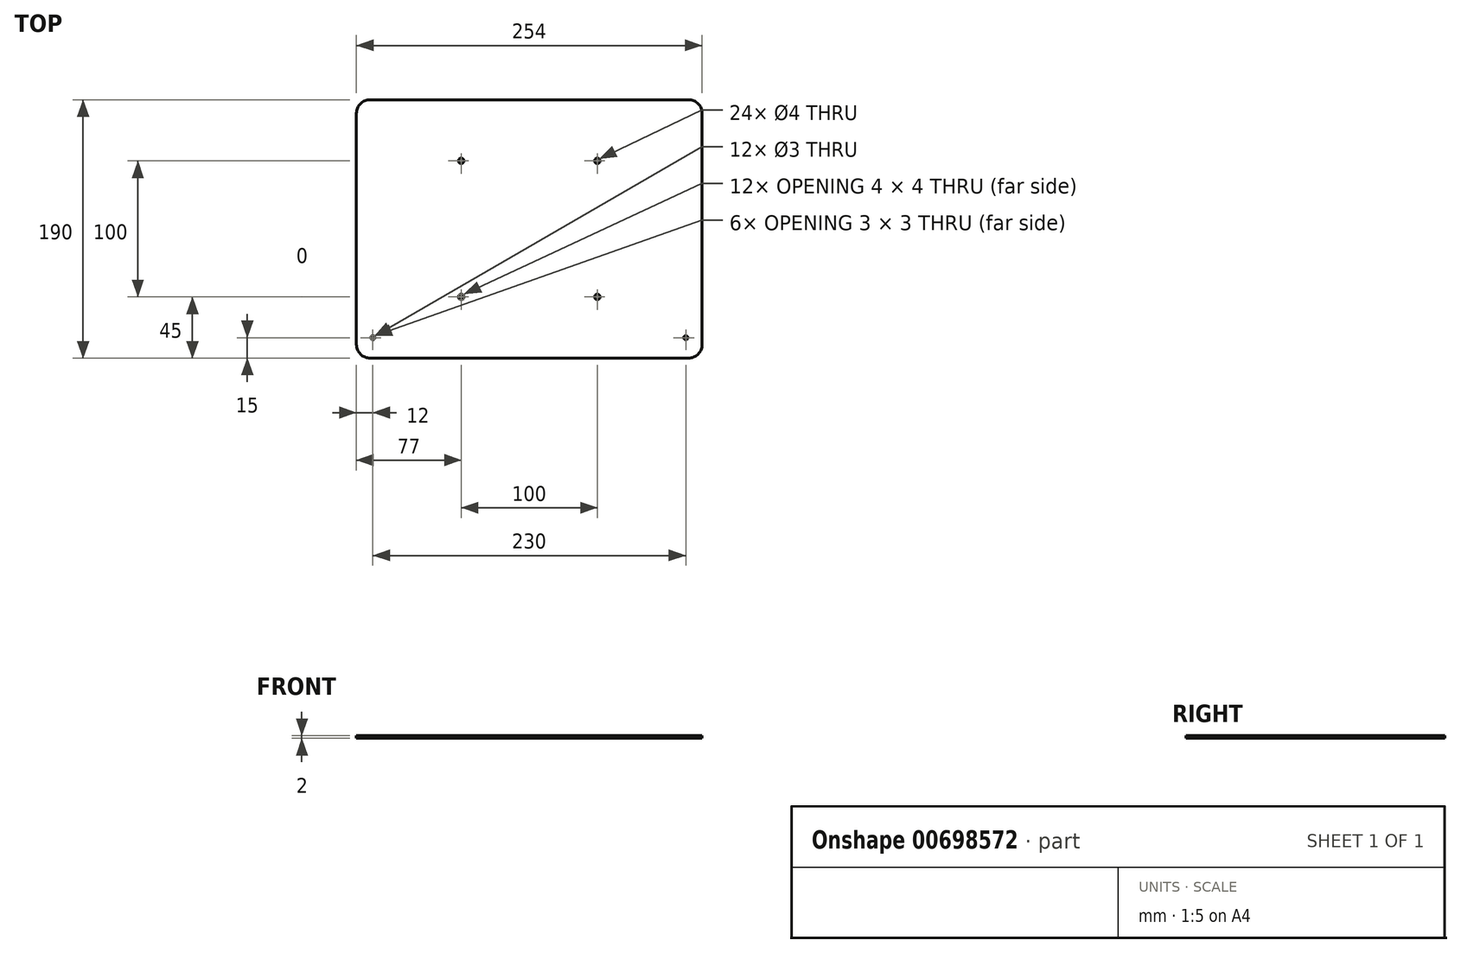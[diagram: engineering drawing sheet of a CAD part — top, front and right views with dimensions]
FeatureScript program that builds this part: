
annotation { "Feature Type Name" : "Feature", "Feature Type Description" : "" }
export const myFeature = defineFeature(function(context is Context, id is Id, definition is map)
    precondition{}
    {
        {
            var Q0;
            Q0=qCreatedBy(makeId("Top.planeOp"),FACE);
            var sketch = newSketch(context, id + "F0", { "sketchPlane" : qUnion([Q0])});
            skLineSegment(sketch, "E0.bottom", {"start": v(-127, 95) * mm, "end": v(127, 95) * mm});
            skLineSegment(sketch, "E0.top", {"start": v(-127, -95) * mm, "end": v(127, -95) * mm});
            skLineSegment(sketch, "E0.left", {"start": v(-127, 95) * mm, "end": v(-127, -95) * mm});
            skLineSegment(sketch, "E0.right", {"start": v(127, 95) * mm, "end": v(127, -95) * mm});
            skPoint(sketch, "E0.middle", {"position": v(0, 0) * mm});
            skSolve(sketch);
        }
        {
            var Q0;
            Q0=makeQuery(id+"F0.imprint","IMPRINT",FACE,{"disambiguationData":[TD([[makeQuery(id+"F0.imprint","IMPRINT",EDGE,{"derivedFrom":sQuery(id+"F0.wireOp",EDGE,"E0.bottom")}),-1.0]])]});
            extrude(context, id + "F1", {"entities" : qUnion([Q0]), "depth" : 2 * mm, "offsetDistance" : 25 * mm});
        }
        {
            var Q0;
            Q0=makeQuery(id+"F1.opExtrude","SWEPT_EDGE",EDGE,{"disambiguationData":[OSD([sQuery(id+"F0.wireOp",EDGE,"E0.top"),sQuery(id+"F0.wireOp",EDGE,"E0.left")])]});
            var Q1;
            Q1=makeQuery(id+"F1.opExtrude","SWEPT_EDGE",EDGE,{"disambiguationData":[OSD([sQuery(id+"F0.wireOp",EDGE,"E0.top"),sQuery(id+"F0.wireOp",EDGE,"E0.right")])]});
            var Q2;
            Q2=makeQuery(id+"F1.opExtrude","SWEPT_EDGE",EDGE,{"disambiguationData":[OSD([sQuery(id+"F0.wireOp",EDGE,"E0.bottom"),sQuery(id+"F0.wireOp",EDGE,"E0.left")])]});
            var Q3;
            Q3=makeQuery(id+"F1.opExtrude","SWEPT_EDGE",EDGE,{"disambiguationData":[OSD([sQuery(id+"F0.wireOp",EDGE,"E0.bottom"),sQuery(id+"F0.wireOp",EDGE,"E0.right")])]});
            fillet(context, id + "F2", {"entities" : qUnion([Q0, Q1, Q2, Q3]), "radius" : 10 * mm, "tangentPropagation" : true, "allowEdgeOverflow" : false});
        }
        {
            var Q0;
            Q0=makeQuery(id+"F1.opExtrude","CAP_FACE",FACE,{"disambiguationData":[OSD([sQuery(id+"F0.wireOp",EDGE,"E0.bottom"),sQuery(id+"F0.wireOp",EDGE,"E0.top"),sQuery(id+"F0.wireOp",EDGE,"E0.left"),sQuery(id+"F0.wireOp",EDGE,"E0.right")])],"isStart":false});
            var sketch = newSketch(context, id + "F3", { "sketchPlane" : qUnion([Q0])});
            skPoint(sketch, "E1", {"position": v(-50, 50) * mm});
            skPoint(sketch, "E2.0.1.0", {"position": v(-50, -50) * mm});
            skPoint(sketch, "E2.1.0.0", {"position": v(50, 50) * mm});
            skPoint(sketch, "E2.1.1.0", {"position": v(50, -50) * mm});
            skPoint(sketch, "E2.2.0.0", {"position": v(150, 50) * mm});
            skPoint(sketch, "E2.2.1.0", {"position": v(150, -50) * mm});
            skLineSegment(sketch, "E2.direction1", {"start": v(-50, 50) * mm, "end": v(50, 50) * mm, "construction": true});
            skLineSegment(sketch, "E2.direction2", {"start": v(-50, 50) * mm, "end": v(-50, -50) * mm, "construction": true});
            skSolve(sketch);
        }
        {
            var Q0;
            Q0=sQuery(id+"F3.wireOp",VERTEX,"E1");
            var Q1;
            Q1=sQuery(id+"F3.wireOp",VERTEX,"E2.1.0.0");
            var Q2;
            Q2=sQuery(id+"F3.wireOp",VERTEX,"E2.1.1.0");
            var Q3;
            Q3=sQuery(id+"F3.wireOp",VERTEX,"E2.0.1.0");
            var Q4;
            Q4=makeQuery(id+"F1.opExtrude","SWEPT_BODY",BODY,{"disambiguationData":[OSD([sQuery(id+"F0.wireOp",EDGE,"E0.bottom"),sQuery(id+"F0.wireOp",EDGE,"E0.top"),sQuery(id+"F0.wireOp",EDGE,"E0.left"),sQuery(id+"F0.wireOp",EDGE,"E0.right")])]});
            hole(context, id + "F4", {"style" : HoleStyle.SIMPLE, "endStyle" : HoleEndStyle.THROUGH, "holeDiameter" : 4 * mm, "majorDiameter" : 5 * mm, "isTappedThrough" : true, "tappedDepth" : 12 * mm, "tapClearance" : 3, "locations" : qUnion([Q0, Q1, Q2, Q3]), "scope" : qUnion([Q4])});
        }
        {
            var Q0;
            Q0=makeQuery(id+"F1.opExtrude","CAP_FACE",FACE,{"disambiguationData":[OSD([sQuery(id+"F0.wireOp",EDGE,"E0.bottom"),sQuery(id+"F0.wireOp",EDGE,"E0.top"),sQuery(id+"F0.wireOp",EDGE,"E0.left"),sQuery(id+"F0.wireOp",EDGE,"E0.right")])],"isStart":false});
            var sketch = newSketch(context, id + "F5", { "sketchPlane" : qUnion([Q0])});
            skPoint(sketch, "E3", {"position": v(-115, -80) * mm});
            skPoint(sketch, "E4", {"position": v(115, -80) * mm});
            skSolve(sketch);
        }
        {
            var Q0;
            Q0=sQuery(id+"F5.wireOp",VERTEX,"E3");
            var Q1;
            Q1=sQuery(id+"F5.wireOp",VERTEX,"E4");
            var Q2;
            Q2=makeQuery(id+"F1.opExtrude","SWEPT_BODY",BODY,{"disambiguationData":[OSD([sQuery(id+"F0.wireOp",EDGE,"E0.bottom"),sQuery(id+"F0.wireOp",EDGE,"E0.top"),sQuery(id+"F0.wireOp",EDGE,"E0.left"),sQuery(id+"F0.wireOp",EDGE,"E0.right")])]});
            hole(context, id + "F6", {"style" : HoleStyle.SIMPLE, "endStyle" : HoleEndStyle.THROUGH, "holeDiameter" : 3 * mm, "majorDiameter" : 5 * mm, "isTappedThrough" : true, "tappedDepth" : 12 * mm, "tapClearance" : 3, "locations" : qUnion([Q0, Q1]), "scope" : qUnion([Q2])});
        }
    });
